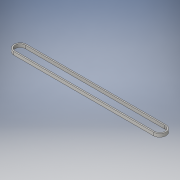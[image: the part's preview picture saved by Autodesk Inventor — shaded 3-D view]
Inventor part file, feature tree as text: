
AUTODESK INVENTOR PART (.ipt)
format: ipt  version: 2016 (Build 200138000, 138)  size: 108,032 bytes
history: native  units: in
note: dims shown in document units (in); Inventor stores cm internally (conversion verified against a paired STEP export)
features: fillet x4, extrude x1, shell x1, sketch x1
ambient origin geometry x8: Origin, YZ Plane, XZ Plane, XY Plane, X Axis, Y Axis, Z Axis, Center Point
bodies: Solid1 (feature_tree)
feature tree (7):
  extrude  "Extrusion1"  Depth=0.25in TaperAngle=0.0deg
  fillet  "Fillet1"  Radius=0.5in
  fillet  "Fillet2"  Radius=0.5in
  fillet  "Fillet3"  Radius=0.5in
  fillet  "Fillet4"  Radius=0.5in
  shell  "Shell1"  Thickness=0.1in
  sketch  "Sketch1"  dims[d0=1.0in d1=0.25in d2=0.0in d3=0.5in d4=0.5in d5=0.5in d6=0.5in d7=0.1in]
